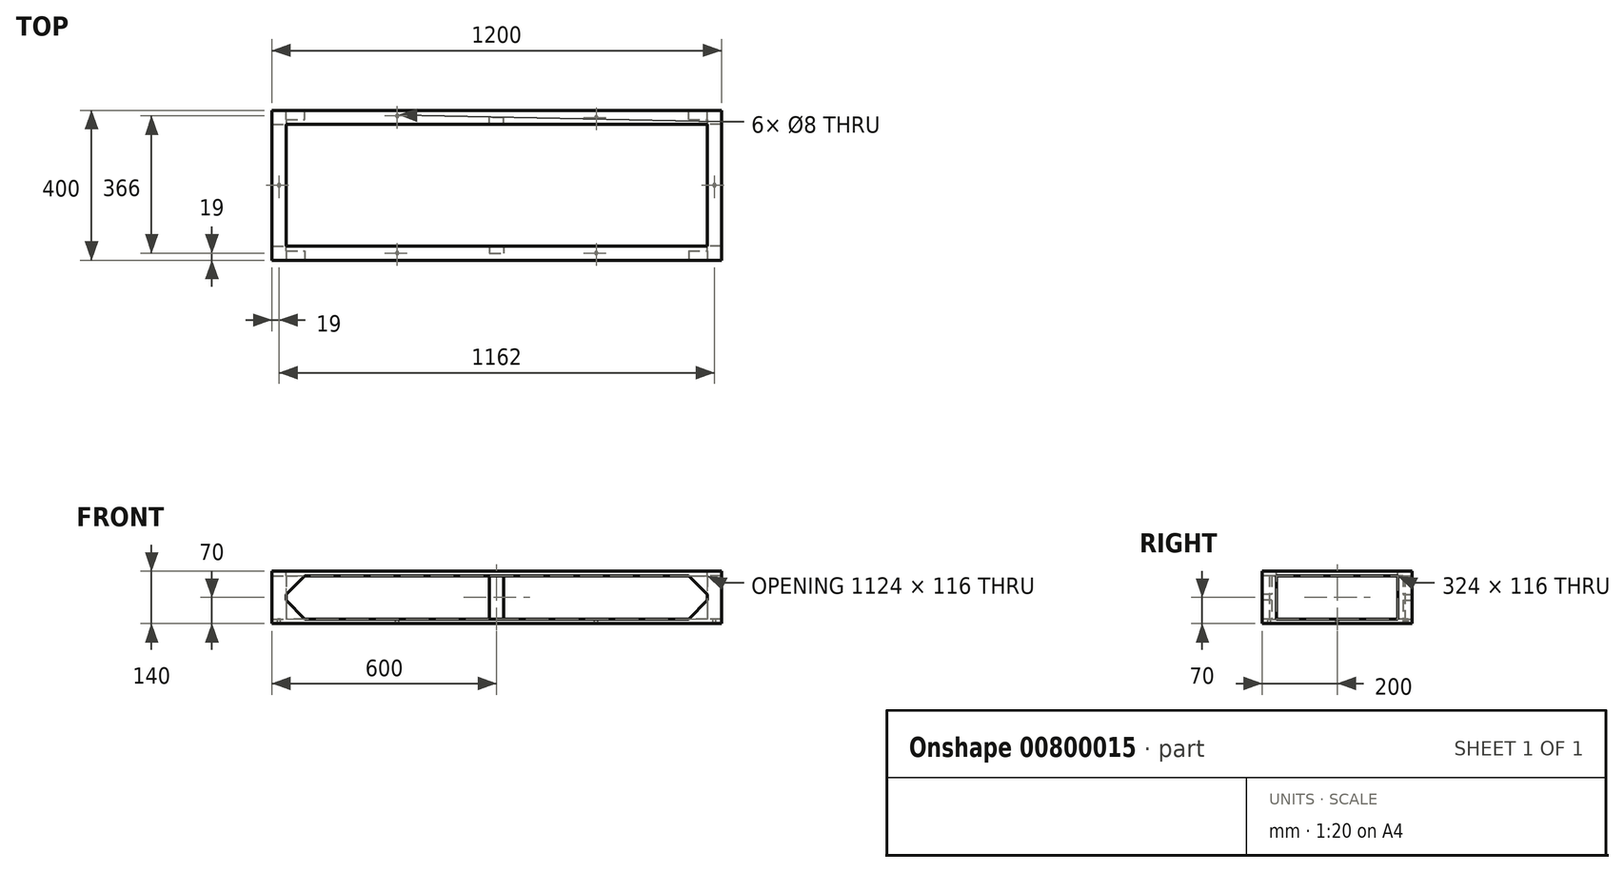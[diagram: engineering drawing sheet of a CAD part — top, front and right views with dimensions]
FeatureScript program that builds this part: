
annotation { "Feature Type Name" : "Feature", "Feature Type Description" : "" }
export const myFeature = defineFeature(function(context is Context, id is Id, definition is map)
    precondition{}
    {
        {
            var Q0;
            Q0=qCreatedBy(makeId("Top.planeOp"),FACE);
            var sketch = newSketch(context, id + "F0", { "sketchPlane" : qUnion([Q0])});
            skLineSegment(sketch, "E0.bottom", {"start": v(600, -200) * mm, "end": v(-600, -200) * mm});
            skLineSegment(sketch, "E0.top", {"start": v(600, 200) * mm, "end": v(-600, 200) * mm});
            skLineSegment(sketch, "E0.left", {"start": v(600, -200) * mm, "end": v(600, 200) * mm});
            skLineSegment(sketch, "E0.right", {"start": v(-600, -200) * mm, "end": v(-600, 200) * mm});
            skPoint(sketch, "E0.middle", {"position": v(0, 0) * mm});
            skSolve(sketch);
        }
        {
            var Q0;
            Q0 = qSketchRegion(id + "F0", true);
            extrude(context, id + "F1", {"entities" : qUnion([Q0]), "depth" : 12 * mm, "offsetDistance" : 25 * mm});
        }
        {
            var Q0;
            Q0=makeQuery(id+"F1.opExtrude","CAP_FACE",FACE,{"disambiguationData":[OSD([sQuery(id+"F0.wireOp",EDGE,"E0.bottom"),sQuery(id+"F0.wireOp",EDGE,"E0.top"),sQuery(id+"F0.wireOp",EDGE,"E0.left"),sQuery(id+"F0.wireOp",EDGE,"E0.right")])],"isStart":false});
            var sketch = newSketch(context, id + "F2", { "sketchPlane" : qUnion([Q0])});
            skLineSegment(sketch, "E1.bottom", {"start": v(-600, 200) * mm, "end": v(-562, 200) * mm});
            skLineSegment(sketch, "E1.top", {"start": v(-600, 162) * mm, "end": v(-562, 162) * mm});
            skLineSegment(sketch, "E1.left", {"start": v(-600, 200) * mm, "end": v(-600, 162) * mm});
            skLineSegment(sketch, "E1.right", {"start": v(-562, 200) * mm, "end": v(-562, 162) * mm});
            skLineSegment(sketch, "E2.bottom", {"start": v(-600, -200) * mm, "end": v(-562, -200) * mm});
            skLineSegment(sketch, "E2.top", {"start": v(-600, -162) * mm, "end": v(-562, -162) * mm});
            skLineSegment(sketch, "E2.left", {"start": v(-600, -200) * mm, "end": v(-600, -162) * mm});
            skLineSegment(sketch, "E2.right", {"start": v(-562, -200) * mm, "end": v(-562, -162) * mm});
            skLineSegment(sketch, "E3", {"start": v(0, 200) * mm, "end": v(0, -200) * mm, "construction": true});
            skLineSegment(sketch, "E4.MirrorCS", {"start": v(600, 162) * mm, "end": v(562, 162) * mm});
            skLineSegment(sketch, "E5.MirrorCS", {"start": v(562, 200) * mm, "end": v(562, 162) * mm});
            skLineSegment(sketch, "E6.MirrorCS", {"start": v(600, 200) * mm, "end": v(562, 200) * mm});
            skLineSegment(sketch, "E7.MirrorCS", {"start": v(600, 200) * mm, "end": v(600, 162) * mm});
            skLineSegment(sketch, "E8.MirrorCS", {"start": v(600, -162) * mm, "end": v(562, -162) * mm});
            skLineSegment(sketch, "E9.MirrorCS", {"start": v(600, -200) * mm, "end": v(600, -162) * mm});
            skLineSegment(sketch, "E10.MirrorCS", {"start": v(600, -200) * mm, "end": v(562, -200) * mm});
            skLineSegment(sketch, "E11.MirrorCS", {"start": v(562, -200) * mm, "end": v(562, -162) * mm});
            skSolve(sketch);
        }
        {
            var Q0;
            Q0=makeQuery(id+"F2.imprint","IMPRINT",FACE,{"disambiguationData":[TD([[makeQuery(id+"F2.imprint","IMPRINT",EDGE,{"derivedFrom":sQuery(id+"F2.wireOp",EDGE,"E1.bottom")}),1.0]])]});
            var Q1;
            Q1=makeQuery(id+"F2.imprint","IMPRINT",FACE,{"disambiguationData":[TD([[makeQuery(id+"F2.imprint","IMPRINT",EDGE,{"derivedFrom":sQuery(id+"F2.wireOp",EDGE,"E4.MirrorCS")}),-1.0]])]});
            var Q2;
            Q2=makeQuery(id+"F2.imprint","IMPRINT",FACE,{"disambiguationData":[TD([[makeQuery(id+"F2.imprint","IMPRINT",EDGE,{"derivedFrom":sQuery(id+"F2.wireOp",EDGE,"E8.MirrorCS")}),1.0]])]});
            var Q3;
            Q3=makeQuery(id+"F2.imprint","IMPRINT",FACE,{"disambiguationData":[TD([[makeQuery(id+"F2.imprint","IMPRINT",EDGE,{"derivedFrom":sQuery(id+"F2.wireOp",EDGE,"E2.bottom")}),-1.0]])]});
            extrude(context, id + "F3", {"entities" : qUnion([Q0, Q1, Q2, Q3]), "operationType" : NewBodyOperationType.ADD, "depth" : 128 * mm, "offsetDistance" : 25 * mm});
        }
        {
            var Q0;
            Q0=makeQuery(id+"F3.opExtrude","CAP_FACE",FACE,{"disambiguationData":[OSD([sQuery(id+"F2.wireOp",EDGE,"E1.bottom"),sQuery(id+"F2.wireOp",EDGE,"E1.top"),sQuery(id+"F2.wireOp",EDGE,"E1.left"),sQuery(id+"F2.wireOp",EDGE,"E1.right")])],"isStart":false});
            var sketch = newSketch(context, id + "F4", { "sketchPlane" : qUnion([Q0])});
            skLineSegment(sketch, "E12.bottom", {"start": v(-600, 200) * mm, "end": v(600, 200) * mm});
            skLineSegment(sketch, "E12.top", {"start": v(-600, -200) * mm, "end": v(600, -200) * mm});
            skLineSegment(sketch, "E12.left", {"start": v(-600, 200) * mm, "end": v(-600, -200) * mm});
            skLineSegment(sketch, "E12.right", {"start": v(600, 200) * mm, "end": v(600, -200) * mm});
            skSolve(sketch);
        }
        {
            var Q0;
            {var subQ2=sQuery(id+"F4.wireOp",EDGE,"E12.top");Q0=makeQuery(id+"F4.imprint","IMPRINT",FACE,{"disambiguationData":[TD([[makeQuery(id+"F4.imprint","IMPRINT",EDGE,{"derivedFrom":subQ2}),1.0]])]});}
            extrude(context, id + "F5", {"entities" : qUnion([Q0]), "operationType" : NewBodyOperationType.ADD, "oppositeDirection" : true, "depth" : 12 * mm, "offsetDistance" : 25 * mm});
        }
        {
            var Q0;
            Q0=makeQuery(id+"F5.boolean.opBoolean","MERGE",FACE,{"derivedFrom":[makeQuery(id+"F3.boolean.opBoolean","MERGE",FACE,{"derivedFrom":[makeQuery(id+"F1.opExtrude","SWEPT_FACE",FACE,{"disambiguationData":[OSD([sQuery(id+"F0.wireOp",EDGE,"E0.bottom")])]}),makeQuery(id+"F3.opExtrude","SWEPT_FACE",FACE,{"disambiguationData":[OSD([sQuery(id+"F2.wireOp",EDGE,"E2.bottom")])]}),makeQuery(id+"F3.opExtrude","SWEPT_FACE",FACE,{"disambiguationData":[OSD([sQuery(id+"F2.wireOp",EDGE,"E10.MirrorCS")])]})]}),makeQuery(id+"F5.opExtrude","SWEPT_FACE",FACE,{"disambiguationData":[OSD([sQuery(id+"F4.wireOp",EDGE,"E12.top")])]})]});
            var sketch = newSketch(context, id + "F6", { "sketchPlane" : qUnion([Q0])});
            skLineSegment(sketch, "E13", {"start": v(-562, 62) * mm, "end": v(-512, 12) * mm});
            skLineSegment(sketch, "E14", {"start": v(-512, 12) * mm, "end": v(-562, 12) * mm});
            skLineSegment(sketch, "E15", {"start": v(-562, 12) * mm, "end": v(-562, 62) * mm});
            skLineSegment(sketch, "E16", {"start": v(0, 128) * mm, "end": v(0, 0) * mm, "construction": true});
            skLineSegment(sketch, "E17", {"start": v(-562, 70) * mm, "end": v(562, 70) * mm, "construction": true});
            skLineSegment(sketch, "E18.MirrorCS", {"start": v(-562, 128) * mm, "end": v(-562, 78) * mm});
            skLineSegment(sketch, "E19.MirrorCS", {"start": v(-562, 78) * mm, "end": v(-512, 128) * mm});
            skLineSegment(sketch, "E20.MirrorCS", {"start": v(-512, 128) * mm, "end": v(-562, 128) * mm});
            skLineSegment(sketch, "E21.MirrorCS", {"start": v(562, 128) * mm, "end": v(562, 78) * mm});
            skLineSegment(sketch, "E22.MirrorCS", {"start": v(512, 128) * mm, "end": v(562, 128) * mm});
            skLineSegment(sketch, "E23.MirrorCS", {"start": v(562, 78) * mm, "end": v(512, 128) * mm});
            skLineSegment(sketch, "E24.MirrorCS", {"start": v(562, 12) * mm, "end": v(562, 62) * mm});
            skLineSegment(sketch, "E25.MirrorCS", {"start": v(512, 12) * mm, "end": v(562, 12) * mm});
            skLineSegment(sketch, "E26.MirrorCS", {"start": v(562, 62) * mm, "end": v(512, 12) * mm});
            skSolve(sketch);
        }
        {
            var Q0;
            Q0=makeQuery(id+"F6.imprint","IMPRINT",FACE,{"disambiguationData":[TD([[makeQuery(id+"F6.imprint","IMPRINT",EDGE,{"derivedFrom":sQuery(id+"F6.wireOp",EDGE,"E18.MirrorCS")}),1.0]])]});
            var Q1;
            Q1=makeQuery(id+"F6.imprint","IMPRINT",FACE,{"disambiguationData":[TD([[makeQuery(id+"F6.imprint","IMPRINT",EDGE,{"derivedFrom":sQuery(id+"F6.wireOp",EDGE,"E13")}),-1.0]])]});
            var Q2;
            Q2=makeQuery(id+"F6.imprint","IMPRINT",FACE,{"disambiguationData":[TD([[makeQuery(id+"F6.imprint","IMPRINT",EDGE,{"derivedFrom":sQuery(id+"F6.wireOp",EDGE,"E24.MirrorCS")}),-1.0]])]});
            var Q3;
            Q3=makeQuery(id+"F6.imprint","IMPRINT",FACE,{"disambiguationData":[TD([[makeQuery(id+"F6.imprint","IMPRINT",EDGE,{"derivedFrom":sQuery(id+"F6.wireOp",EDGE,"E21.MirrorCS")}),-1.0]])]});
            extrude(context, id + "F7", {"entities" : qUnion([Q0, Q1, Q2, Q3]), "oppositeDirection" : true, "depth" : 25 * mm, "offsetDistance" : 25 * mm});
        }
        {
            var Q0;
            Q0=makeQuery(id+"F7.opExtrude","SWEPT_BODY",BODY,{"disambiguationData":[OSD([sQuery(id+"F6.wireOp",EDGE,"E18.MirrorCS"),sQuery(id+"F6.wireOp",EDGE,"E19.MirrorCS"),sQuery(id+"F6.wireOp",EDGE,"E20.MirrorCS")])]});
            var Q1;
            Q1=makeQuery(id+"F7.opExtrude","SWEPT_BODY",BODY,{"disambiguationData":[OSD([sQuery(id+"F6.wireOp",EDGE,"E13"),sQuery(id+"F6.wireOp",EDGE,"E14"),sQuery(id+"F6.wireOp",EDGE,"E15")])]});
            var Q2;
            Q2=makeQuery(id+"F7.opExtrude","SWEPT_BODY",BODY,{"disambiguationData":[OSD([sQuery(id+"F6.wireOp",EDGE,"E24.MirrorCS"),sQuery(id+"F6.wireOp",EDGE,"E25.MirrorCS"),sQuery(id+"F6.wireOp",EDGE,"E26.MirrorCS")])]});
            var Q3;
            Q3=makeQuery(id+"F7.opExtrude","SWEPT_BODY",BODY,{"disambiguationData":[OSD([sQuery(id+"F6.wireOp",EDGE,"E21.MirrorCS"),sQuery(id+"F6.wireOp",EDGE,"E22.MirrorCS"),sQuery(id+"F6.wireOp",EDGE,"E23.MirrorCS")])]});
            var Q4;
            Q4=qCreatedBy(makeId("Front.planeOp"),FACE);
            mirror(context, id + "F8", {"operationType" : NewBodyOperationType.ADD, "entities" : qUnion([Q0, Q1, Q2, Q3]), "mirrorPlane" : qUnion([Q4])});
        }
        {
            var Q0;
            Q0=makeQuery(id+"F1.opExtrude","CAP_FACE",FACE,{"disambiguationData":[OSD([sQuery(id+"F0.wireOp",EDGE,"E0.bottom"),sQuery(id+"F0.wireOp",EDGE,"E0.top"),sQuery(id+"F0.wireOp",EDGE,"E0.left"),sQuery(id+"F0.wireOp",EDGE,"E0.right")])],"isStart":false});
            var sketch = newSketch(context, id + "F9", { "sketchPlane" : qUnion([Q0])});
            skLineSegment(sketch, "E27.bottom", {"start": v(19, 200) * mm, "end": v(-19, 200) * mm});
            skLineSegment(sketch, "E27.top", {"start": v(19, 162) * mm, "end": v(-19, 162) * mm});
            skLineSegment(sketch, "E27.left", {"start": v(19, 200) * mm, "end": v(19, 162) * mm});
            skLineSegment(sketch, "E27.right", {"start": v(-19, 200) * mm, "end": v(-19, 162) * mm});
            skPoint(sketch, "E27.middle", {"position": v(0, 181) * mm});
            skLineSegment(sketch, "E28.bottom", {"start": v(19, -200) * mm, "end": v(-19, -200) * mm});
            skLineSegment(sketch, "E28.top", {"start": v(19, -162) * mm, "end": v(-19, -162) * mm});
            skLineSegment(sketch, "E28.left", {"start": v(19, -200) * mm, "end": v(19, -162) * mm});
            skLineSegment(sketch, "E28.right", {"start": v(-19, -200) * mm, "end": v(-19, -162) * mm});
            skPoint(sketch, "E28.middle", {"position": v(0, -181) * mm});
            skSolve(sketch);
        }
        {
            var Q0;
            Q0=makeQuery(id+"F9.imprint","IMPRINT",FACE,{"disambiguationData":[TD([[makeQuery(id+"F9.imprint","IMPRINT",EDGE,{"derivedFrom":sQuery(id+"F9.wireOp",EDGE,"E28.bottom")}),-1.0]])]});
            var Q1;
            Q1=makeQuery(id+"F9.imprint","IMPRINT",FACE,{"disambiguationData":[TD([[makeQuery(id+"F9.imprint","IMPRINT",EDGE,{"derivedFrom":sQuery(id+"F9.wireOp",EDGE,"E27.bottom")}),1.0]])]});
            extrude(context, id + "F10", {"entities" : qUnion([Q0, Q1]), "operationType" : NewBodyOperationType.ADD, "depth" : 120 * mm, "offsetDistance" : 25 * mm});
        }
        {
            var Q0;
            Q0=makeQuery(id+"F1.opExtrude","CAP_FACE",FACE,{"disambiguationData":[OSD([sQuery(id+"F0.wireOp",EDGE,"E0.bottom"),sQuery(id+"F0.wireOp",EDGE,"E0.top"),sQuery(id+"F0.wireOp",EDGE,"E0.left"),sQuery(id+"F0.wireOp",EDGE,"E0.right")])],"isStart":false});
            var sketch = newSketch(context, id + "F11", { "sketchPlane" : qUnion([Q0])});
            skCircle(sketch, "E29", {"center": v(-265.5, -181) * mm, "radius": 4 * mm});
            skPoint(sketch, "E29.centerSnap0", {"position": v(19, -181) * mm});
            skPoint(sketch, "E29.centerSnap1", {"position": v(-265.5, -200) * mm});
            skCircle(sketch, "E30", {"center": v(-581, 0) * mm, "radius": 4 * mm});
            skPoint(sketch, "E30.centerSnap0", {"position": v(-600, 0) * mm});
            skCircle(sketch, "E31", {"center": v(-265.5, 185) * mm, "radius": 4 * mm});
            skPoint(sketch, "E31.centerSnap0", {"position": v(-265.5, 200) * mm});
            skCircle(sketch, "E32", {"center": v(265.5, 181) * mm, "radius": 4 * mm});
            skPoint(sketch, "E32.centerSnap0", {"position": v(265.5, 200) * mm});
            skCircle(sketch, "E33", {"center": v(265.5, -181) * mm, "radius": 4 * mm});
            skPoint(sketch, "E33.centerSnap0", {"position": v(265.5, -200) * mm});
            skCircle(sketch, "E34", {"center": v(581, 0) * mm, "radius": 4 * mm});
            skPoint(sketch, "E34.centerSnap0", {"position": v(600, 0) * mm});
            skSolve(sketch);
        }
        {
            var Q0;
            Q0 = qSketchRegion(id + "F11", true);
            extrude(context, id + "F12", {"entities" : qUnion([Q0]), "operationType" : NewBodyOperationType.REMOVE, "oppositeDirection" : true, "depth" : 25 * mm, "offsetDistance" : 25 * mm});
        }
        {
            var Q0;
            {var subQ0=sQuery(id+"F2.wireOp",EDGE,"E1.right");var subQ1=sQuery(id+"F2.wireOp",EDGE,"E1.top");Q0=makeQuery(id+"F5.boolean.opBoolean","MERGE",FACE,{"derivedFrom":[makeQuery(id+"F3.opExtrude","CAP_FACE",FACE,{"disambiguationData":[OSD([sQuery(id+"F2.wireOp",EDGE,"E1.bottom"),subQ1,sQuery(id+"F2.wireOp",EDGE,"E1.left"),subQ0])],"isStart":false}),makeQuery(id+"F3.opExtrude","CAP_FACE",FACE,{"disambiguationData":[OSD([sQuery(id+"F2.wireOp",EDGE,"E2.bottom"),sQuery(id+"F2.wireOp",EDGE,"E2.top"),sQuery(id+"F2.wireOp",EDGE,"E2.left"),sQuery(id+"F2.wireOp",EDGE,"E2.right")])],"isStart":false}),makeQuery(id+"F3.opExtrude","CAP_FACE",FACE,{"disambiguationData":[OSD([sQuery(id+"F2.wireOp",EDGE,"E4.MirrorCS"),sQuery(id+"F2.wireOp",EDGE,"E5.MirrorCS"),sQuery(id+"F2.wireOp",EDGE,"E6.MirrorCS"),sQuery(id+"F2.wireOp",EDGE,"E7.MirrorCS")])],"isStart":false}),makeQuery(id+"F3.opExtrude","CAP_FACE",FACE,{"disambiguationData":[OSD([sQuery(id+"F2.wireOp",EDGE,"E8.MirrorCS"),sQuery(id+"F2.wireOp",EDGE,"E9.MirrorCS"),sQuery(id+"F2.wireOp",EDGE,"E10.MirrorCS"),sQuery(id+"F2.wireOp",EDGE,"E11.MirrorCS")])],"isStart":false}),makeQuery(id+"F5.opExtrude","CAP_FACE",FACE,{"disambiguationData":[OSD([subQ1,subQ0,sQuery(id+"F4.wireOp",EDGE,"E12.bottom"),sQuery(id+"F4.wireOp",EDGE,"E12.top"),sQuery(id+"F4.wireOp",EDGE,"E12.left"),sQuery(id+"F4.wireOp",EDGE,"E12.right")])],"isStart":true})]});}
            var sketch = newSketch(context, id + "F13", { "sketchPlane" : qUnion([Q0])});
            skLineSegment(sketch, "E35.bottom", {"start": v(-562, -162) * mm, "end": v(562, -162) * mm});
            skLineSegment(sketch, "E35.top", {"start": v(-562, 162) * mm, "end": v(562, 162) * mm});
            skLineSegment(sketch, "E35.left", {"start": v(-562, -162) * mm, "end": v(-562, 162) * mm});
            skLineSegment(sketch, "E35.right", {"start": v(562, -162) * mm, "end": v(562, 162) * mm});
            skPoint(sketch, "E35.middle", {"position": v(0, 0) * mm});
            skSolve(sketch);
        }
        {
            var Q0;
            Q0=makeQuery(id+"F13.imprint","IMPRINT",FACE,{"disambiguationData":[TD([[makeQuery(id+"F13.imprint","IMPRINT",EDGE,{"derivedFrom":sQuery(id+"F13.wireOp",EDGE,"E35.bottom")}),1.0]])]});
            extrude(context, id + "F14", {"entities" : qUnion([Q0]), "operationType" : NewBodyOperationType.REMOVE, "oppositeDirection" : true, "depth" : 25 * mm, "offsetDistance" : 25 * mm});
        }
        {
            var Q0;
            Q0=makeQuery(id+"F10.boolean.opBoolean","MERGE",FACE,{"derivedFrom":[makeQuery(id+"F8.boolean.opBoolean","MERGE",FACE,{"derivedFrom":[makeQuery(id+"F5.boolean.opBoolean","MERGE",FACE,{"derivedFrom":[makeQuery(id+"F3.boolean.opBoolean","MERGE",FACE,{"derivedFrom":[makeQuery(id+"F1.opExtrude","SWEPT_FACE",FACE,{"disambiguationData":[OSD([sQuery(id+"F0.wireOp",EDGE,"E0.bottom")])]}),makeQuery(id+"F3.opExtrude","SWEPT_FACE",FACE,{"disambiguationData":[OSD([sQuery(id+"F2.wireOp",EDGE,"E2.bottom")])]}),makeQuery(id+"F3.opExtrude","SWEPT_FACE",FACE,{"disambiguationData":[OSD([sQuery(id+"F2.wireOp",EDGE,"E10.MirrorCS")])]})]}),makeQuery(id+"F5.opExtrude","SWEPT_FACE",FACE,{"disambiguationData":[OSD([sQuery(id+"F4.wireOp",EDGE,"E12.top")])]})]}),makeQuery(id+"F7.opExtrude","CAP_FACE",FACE,{"disambiguationData":[OSD([sQuery(id+"F6.wireOp",EDGE,"E13"),sQuery(id+"F6.wireOp",EDGE,"E14"),sQuery(id+"F6.wireOp",EDGE,"E15")])],"isStart":true}),makeQuery(id+"F7.opExtrude","CAP_FACE",FACE,{"disambiguationData":[OSD([sQuery(id+"F6.wireOp",EDGE,"E18.MirrorCS"),sQuery(id+"F6.wireOp",EDGE,"E19.MirrorCS"),sQuery(id+"F6.wireOp",EDGE,"E20.MirrorCS")])],"isStart":true}),makeQuery(id+"F7.opExtrude","CAP_FACE",FACE,{"disambiguationData":[OSD([sQuery(id+"F6.wireOp",EDGE,"E21.MirrorCS"),sQuery(id+"F6.wireOp",EDGE,"E22.MirrorCS"),sQuery(id+"F6.wireOp",EDGE,"E23.MirrorCS")])],"isStart":true}),makeQuery(id+"F7.opExtrude","CAP_FACE",FACE,{"disambiguationData":[OSD([sQuery(id+"F6.wireOp",EDGE,"E24.MirrorCS"),sQuery(id+"F6.wireOp",EDGE,"E25.MirrorCS"),sQuery(id+"F6.wireOp",EDGE,"E26.MirrorCS")])],"isStart":true})]}),makeQuery(id+"F10.opExtrude","SWEPT_FACE",FACE,{"disambiguationData":[OSD([sQuery(id+"F9.wireOp",EDGE,"E28.bottom")])]})]});
            var sketch = newSketch(context, id + "F15", { "sketchPlane" : qUnion([Q0])});
            skLineSegment(sketch, "E36.bottom", {"start": v(-19, 128) * mm, "end": v(19, 128) * mm});
            skLineSegment(sketch, "E36.top", {"start": v(-19, 12) * mm, "end": v(19, 12) * mm});
            skLineSegment(sketch, "E36.left", {"start": v(-19, 128) * mm, "end": v(-19, 12) * mm});
            skLineSegment(sketch, "E36.right", {"start": v(19, 128) * mm, "end": v(19, 12) * mm});
            skSolve(sketch);
        }
        {
            var Q0;
            Q0 = qSketchRegion(id + "F15", true);
            extrude(context, id + "F16", {"entities" : qUnion([Q0]), "operationType" : NewBodyOperationType.REMOVE, "oppositeDirection" : true, "depth" : 19 * mm, "offsetDistance" : 25 * mm});
        }
        {
            var Q0;
            Q0=makeQuery(id+"F10.boolean.opBoolean","MERGE",FACE,{"derivedFrom":[makeQuery(id+"F8.boolean.opBoolean","MERGE",FACE,{"derivedFrom":[makeQuery(id+"F5.boolean.opBoolean","MERGE",FACE,{"derivedFrom":[makeQuery(id+"F3.boolean.opBoolean","MERGE",FACE,{"derivedFrom":[makeQuery(id+"F1.opExtrude","SWEPT_FACE",FACE,{"disambiguationData":[OSD([sQuery(id+"F0.wireOp",EDGE,"E0.top")])]}),makeQuery(id+"F3.opExtrude","SWEPT_FACE",FACE,{"disambiguationData":[OSD([sQuery(id+"F2.wireOp",EDGE,"E1.bottom")])]}),makeQuery(id+"F3.opExtrude","SWEPT_FACE",FACE,{"disambiguationData":[OSD([sQuery(id+"F2.wireOp",EDGE,"E6.MirrorCS")])]})]}),makeQuery(id+"F5.opExtrude","SWEPT_FACE",FACE,{"disambiguationData":[OSD([sQuery(id+"F4.wireOp",EDGE,"E12.bottom")])]})]}),makeQuery(id+"F8.opPattern","COPY",FACE,{"derivedFrom":makeQuery(id+"F7.opExtrude","CAP_FACE",FACE,{"disambiguationData":[OSD([sQuery(id+"F6.wireOp",EDGE,"E13"),sQuery(id+"F6.wireOp",EDGE,"E14"),sQuery(id+"F6.wireOp",EDGE,"E15")])],"isStart":true}),"instanceName":"1"}),makeQuery(id+"F8.opPattern","COPY",FACE,{"derivedFrom":makeQuery(id+"F7.opExtrude","CAP_FACE",FACE,{"disambiguationData":[OSD([sQuery(id+"F6.wireOp",EDGE,"E18.MirrorCS"),sQuery(id+"F6.wireOp",EDGE,"E19.MirrorCS"),sQuery(id+"F6.wireOp",EDGE,"E20.MirrorCS")])],"isStart":true}),"instanceName":"1"}),makeQuery(id+"F8.opPattern","COPY",FACE,{"derivedFrom":makeQuery(id+"F7.opExtrude","CAP_FACE",FACE,{"disambiguationData":[OSD([sQuery(id+"F6.wireOp",EDGE,"E21.MirrorCS"),sQuery(id+"F6.wireOp",EDGE,"E22.MirrorCS"),sQuery(id+"F6.wireOp",EDGE,"E23.MirrorCS")])],"isStart":true}),"instanceName":"1"}),makeQuery(id+"F8.opPattern","COPY",FACE,{"derivedFrom":makeQuery(id+"F7.opExtrude","CAP_FACE",FACE,{"disambiguationData":[OSD([sQuery(id+"F6.wireOp",EDGE,"E24.MirrorCS"),sQuery(id+"F6.wireOp",EDGE,"E25.MirrorCS"),sQuery(id+"F6.wireOp",EDGE,"E26.MirrorCS")])],"isStart":true}),"instanceName":"1"})]}),makeQuery(id+"F10.opExtrude","SWEPT_FACE",FACE,{"disambiguationData":[OSD([sQuery(id+"F9.wireOp",EDGE,"E27.bottom")])]})]});
            var sketch = newSketch(context, id + "F17", { "sketchPlane" : qUnion([Q0])});
            skLineSegment(sketch, "E37.bottom", {"start": v(-19, 128) * mm, "end": v(19, 128) * mm});
            skLineSegment(sketch, "E37.top", {"start": v(-19, 12) * mm, "end": v(19, 12) * mm});
            skLineSegment(sketch, "E37.left", {"start": v(-19, 128) * mm, "end": v(-19, 12) * mm});
            skLineSegment(sketch, "E37.right", {"start": v(19, 128) * mm, "end": v(19, 12) * mm});
            skSolve(sketch);
        }
        {
            var Q0;
            Q0 = qSketchRegion(id + "F17", true);
            extrude(context, id + "F18", {"entities" : qUnion([Q0]), "operationType" : NewBodyOperationType.REMOVE, "oppositeDirection" : true, "depth" : 19 * mm, "offsetDistance" : 25 * mm});
        }
    });
